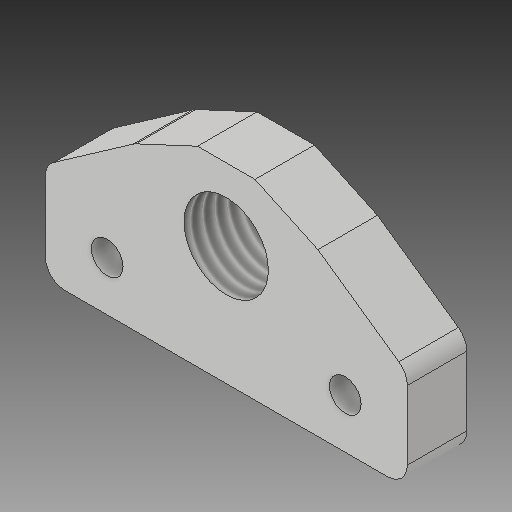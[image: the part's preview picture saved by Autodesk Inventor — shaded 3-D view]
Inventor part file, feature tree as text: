
AUTODESK INVENTOR PART (.ipt)
format: ipt  version: 2017 (Build 210142000, 142)  size: 131,072 bytes
history: native  units: mm
features: other x3, sketch x1
ambient origin geometry x8: Origin, YZ Plane, XZ Plane, XY Plane, X Axis, Y Axis, Z Axis, Center Point
bodies: Solid1 (feature_tree)
feature tree (4):
  other  "pshfit-mount-acrylic_MIR.ipt"
  other  "Solid1::pshfit-mount-acrylic_MIR.ipt"
  other  "TaggingFeature1"
  sketch  "Sketch1"  dims[d0=10.0mm]
